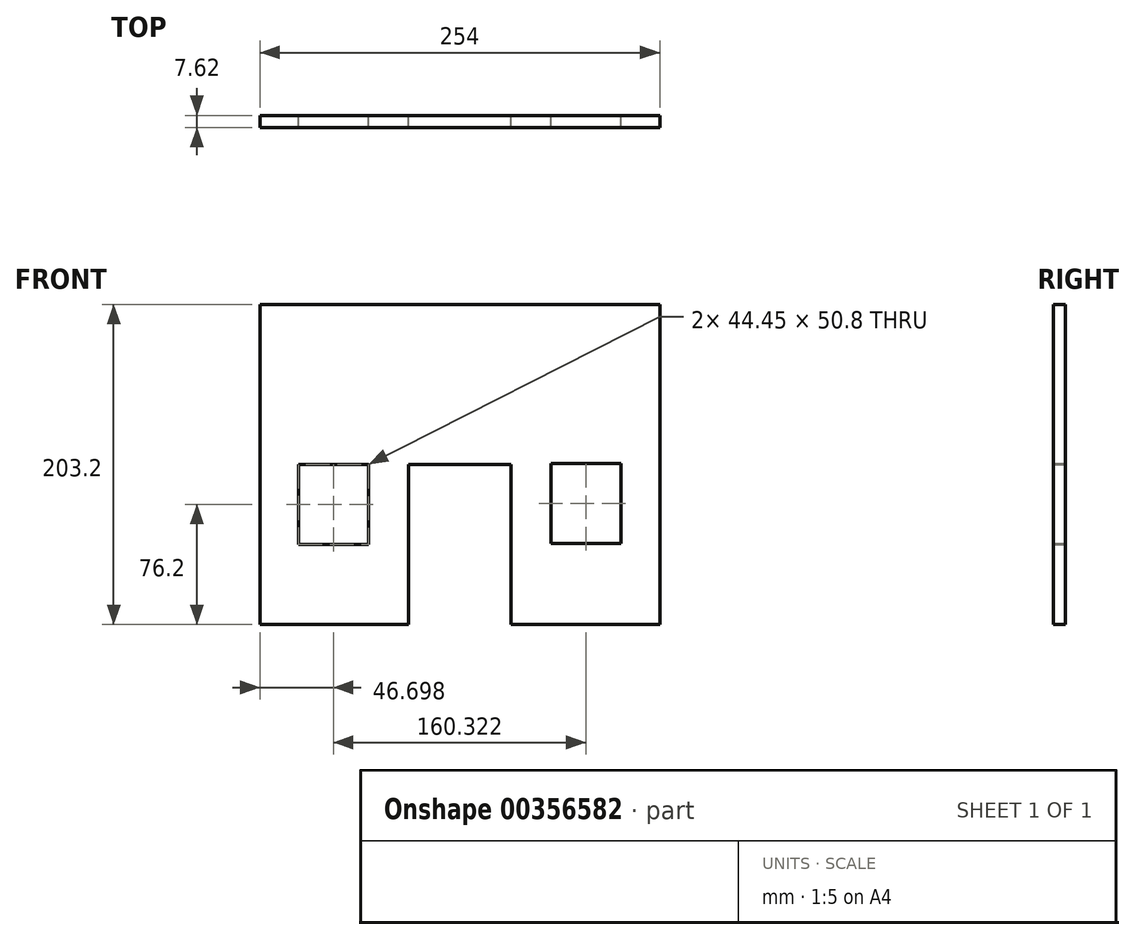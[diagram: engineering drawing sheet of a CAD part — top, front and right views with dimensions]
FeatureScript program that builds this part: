
annotation { "Feature Type Name" : "Feature", "Feature Type Description" : "" }
export const myFeature = defineFeature(function(context is Context, id is Id, definition is map)
    precondition{}
    {
        {
            var Q0;
            Q0=qCreatedBy(makeId("Front.planeOp"),FACE);
            var sketch = newSketch(context, id + "F0", { "sketchPlane" : qUnion([Q0])});
            skLineSegment(sketch, "E0.bottom", {"start": v(-127, 101.6) * mm, "end": v(127, 101.6) * mm});
            skLineSegment(sketch, "E0.top", {"start": v(-127, -101.6) * mm, "end": v(127, -101.6) * mm});
            skLineSegment(sketch, "E0.left", {"start": v(-127, 101.6) * mm, "end": v(-127, -101.6) * mm});
            skLineSegment(sketch, "E0.right", {"start": v(127, 101.6) * mm, "end": v(127, -101.6) * mm});
            skPoint(sketch, "E0.middle", {"position": v(0, 0) * mm});
            skLineSegment(sketch, "E1.bottom", {"start": v(-32.5, 0) * mm, "end": v(32.5, 0) * mm});
            skLineSegment(sketch, "E1.top", {"start": v(-32.5, -101.6) * mm, "end": v(32.5, -101.6) * mm});
            skLineSegment(sketch, "E1.left", {"start": v(-32.5, 0) * mm, "end": v(-32.5, -101.6) * mm});
            skLineSegment(sketch, "E1.right", {"start": v(32.5, 0) * mm, "end": v(32.5, -101.6) * mm});
            skLineSegment(sketch, "E2.bottom", {"start": v(-102.53, 0) * mm, "end": v(-58.08, 0) * mm});
            skLineSegment(sketch, "E2.top", {"start": v(-102.53, -50.8) * mm, "end": v(-58.08, -50.8) * mm});
            skLineSegment(sketch, "E2.left", {"start": v(-102.53, 0) * mm, "end": v(-102.53, -50.8) * mm});
            skLineSegment(sketch, "E2.right", {"start": v(-58.08, 0) * mm, "end": v(-58.08, -50.8) * mm});
            skLineSegment(sketch, "E3.bottom", {"start": v(57.8, 0.55) * mm, "end": v(102.25, 0.55) * mm});
            skLineSegment(sketch, "E3.top", {"start": v(57.8, -50.25) * mm, "end": v(102.25, -50.25) * mm});
            skLineSegment(sketch, "E3.left", {"start": v(57.8, 0.55) * mm, "end": v(57.8, -50.25) * mm});
            skLineSegment(sketch, "E3.right", {"start": v(102.25, 0.55) * mm, "end": v(102.25, -50.25) * mm});
            skSolve(sketch);
        }
        {
            var Q0;
            Q0=makeQuery(id+"F0.imprint","IMPRINT",FACE,{"disambiguationData":[TD([[makeQuery(id+"F0.imprint","IMPRINT",EDGE,{"derivedFrom":sQuery(id+"F0.wireOp",EDGE,"E0.bottom")}),-1.0]])]});
            extrude(context, id + "F1", {"entities" : qUnion([Q0]), "depth" : 7.62 * mm});
        }
    });
